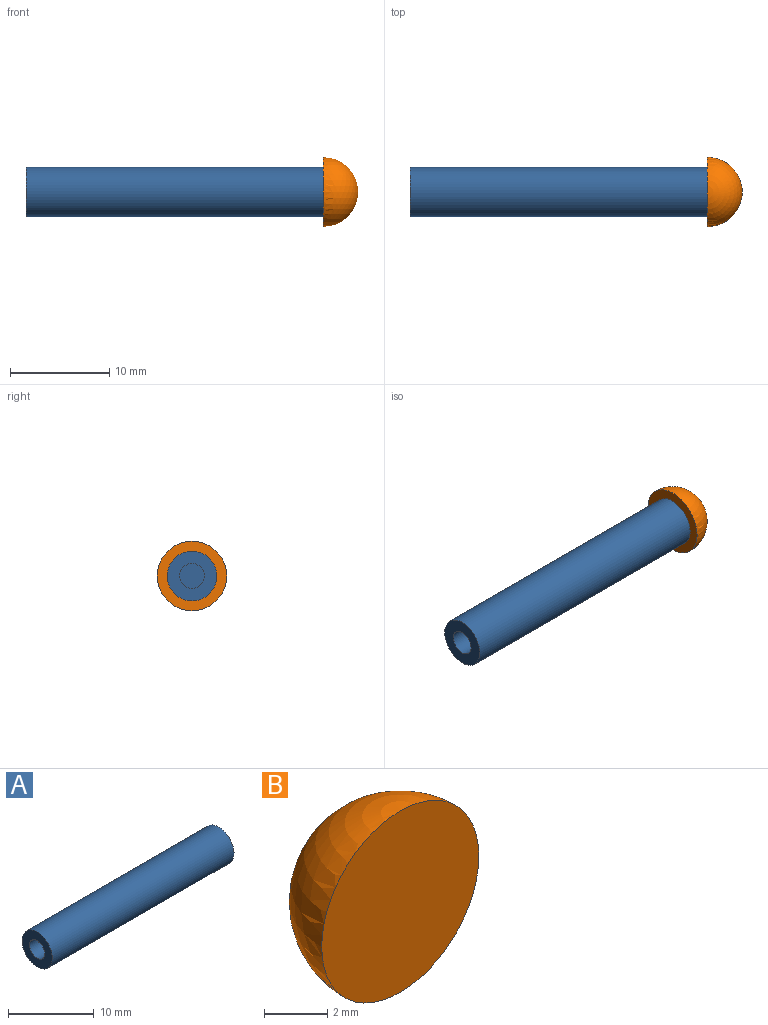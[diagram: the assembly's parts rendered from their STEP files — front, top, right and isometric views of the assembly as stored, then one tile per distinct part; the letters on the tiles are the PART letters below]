
ASSEMBLY  parts=2 mates=1
PART A: 5 faces, bbox 30x5x5 mm
  f0: cylinder r=2.5mm len=30mm, axis (-1,0,0), area 471.2mm2, adj f1,f2
  f1: plane 5x5mm, normal (1,0,0), area 19.6mm2, adj f0
  f2: plane 5x5mm, normal (-1,0,0), area 14.7mm2, adj f0,f3
  f3: cylinder r=1.25mm len=5mm, axis (-1,0,0), area 39.3mm2, adj f2,f4
  f4: plane 2.5x2.5mm, normal (-1,0,0), area 4.9mm2, adj f3
PART B: 2 faces, bbox 7x3.5x7 mm
  f0: sphere r=3.5mm, area 77mm2, adj f1
  f1: plane 7x7mm, normal (0,-1,0), area 38.5mm2, adj f0
PLACE A t=(-10.38,2.96,0.43)mm
PLACE B rot(axis=(0,0,-1),90deg) t=(19.62,2.96,-3.07)mm
MATE fastened B.f1 <-> A.f0  axis (-1,0,0) through (19.62,2.96,0.43)mm
